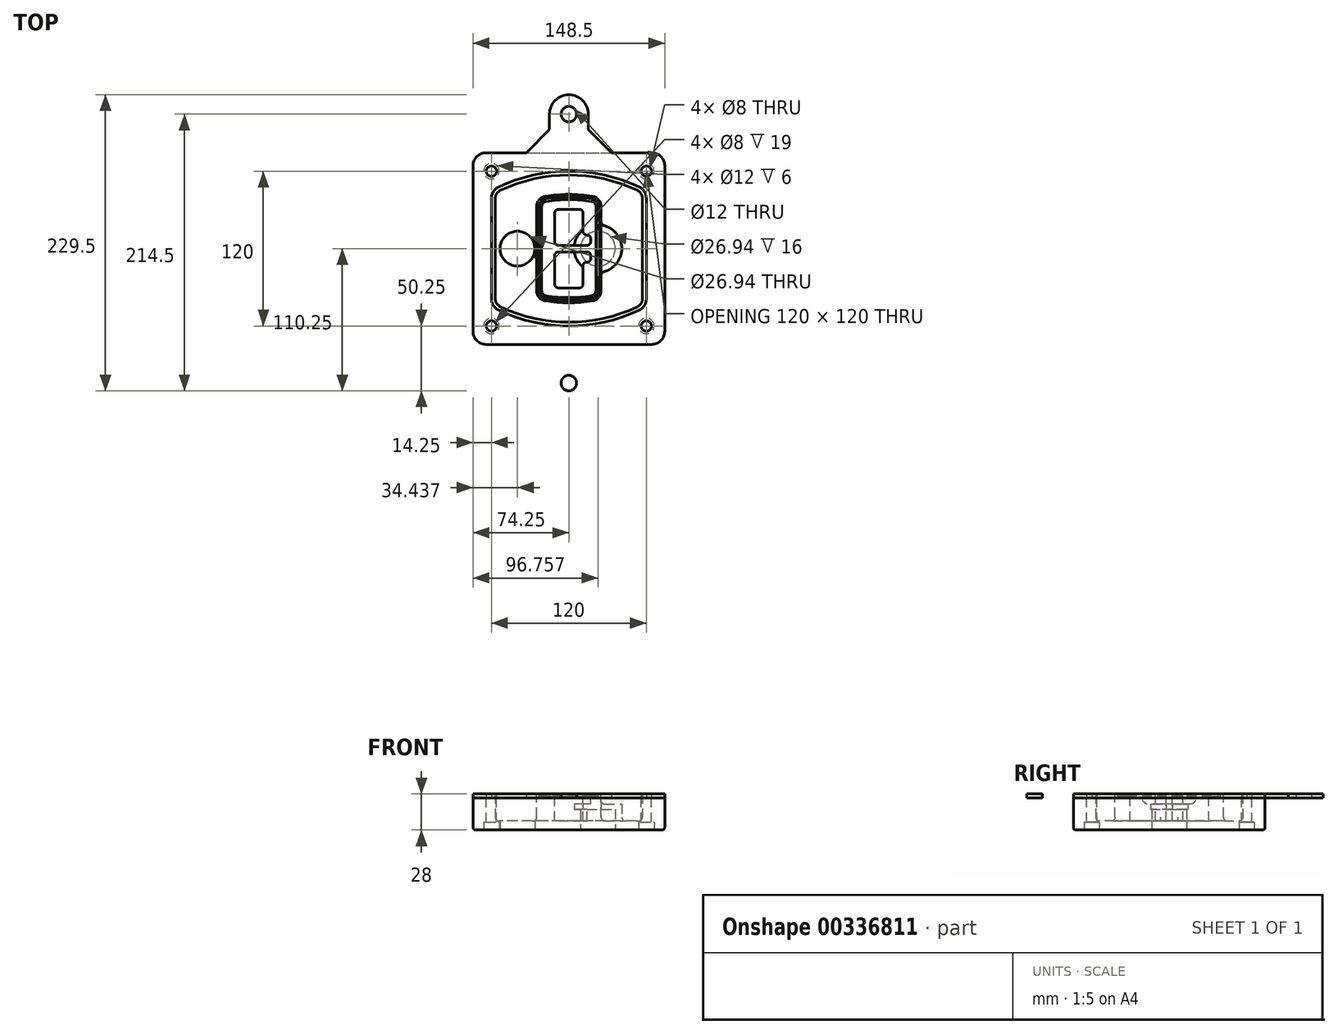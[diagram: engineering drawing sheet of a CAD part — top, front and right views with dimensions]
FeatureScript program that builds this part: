
annotation { "Feature Type Name" : "Feature", "Feature Type Description" : "" }
export const myFeature = defineFeature(function(context is Context, id is Id, definition is map)
    precondition{}
    {
        {
            var Q0;
            Q0=qCreatedBy(makeId("Top.planeOp"),FACE);
            var sketch = newSketch(context, id + "F0", { "sketchPlane" : qUnion([Q0])});
            skPoint(sketch, "E0.rect.middle", {"position": v(0, 0) * mm});
            skLineSegment(sketch, "E1.bottom", {"start": v(-64.25, -74.25) * mm, "end": v(64.25, -74.25) * mm});
            skLineSegment(sketch, "E1.top", {"start": v(-64.25, 74.25) * mm, "end": v(64.25, 74.25) * mm});
            skLineSegment(sketch, "E1.left", {"start": v(-74.25, -64.25) * mm, "end": v(-74.25, 64.25) * mm});
            skLineSegment(sketch, "E1.right", {"start": v(74.25, -64.25) * mm, "end": v(74.25, 64.25) * mm});
            skLineSegment(sketch, "E2", {"start": v(-74.25, 74.25) * mm, "end": v(74.25, -74.25) * mm, "construction": true});
            skLineSegment(sketch, "E3", {"start": v(74.25, 74.25) * mm, "end": v(-74.25, -74.25) * mm, "construction": true});
            skCircle(sketch, "E4", {"center": v(-60, 60) * mm, "radius": 4 * mm});
            skCircle(sketch, "E5", {"center": v(60, 60) * mm, "radius": 4 * mm});
            skCircle(sketch, "E6", {"center": v(60, -60) * mm, "radius": 4 * mm});
            skCircle(sketch, "E7", {"center": v(-60, -60) * mm, "radius": 4 * mm});
            skLineSegment(sketch, "E8", {"start": v(-60, 60) * mm, "end": v(60, 60) * mm, "construction": true});
            skLineSegment(sketch, "E9", {"start": v(60, 60) * mm, "end": v(60, -60) * mm, "construction": true});
            skLineSegment(sketch, "E10", {"start": v(60, -60) * mm, "end": v(-60, -60) * mm, "construction": true});
            skLineSegment(sketch, "E11", {"start": v(-60, -60) * mm, "end": v(-60, 60) * mm, "construction": true});
            skLineSegment(sketch, "E12", {"start": v(-60, 38.83) * mm, "end": v(-60, -38.83) * mm});
            skLineSegment(sketch, "E13", {"start": v(60, 38.83) * mm, "end": v(60, -38.83) * mm});
            skArc(sketch, "E14", {"start": v(54.26, 47.88) * mm, "mid": v(0, 60) * mm, "end": v(-54.26, 47.88) * mm});
            skArc(sketch, "E15", {"start": v(-54.26, -47.88) * mm, "mid": v(0, -60) * mm, "end": v(54.26, -47.88) * mm});
            skLineSegment(sketch, "E16", {"start": v(-60, 0) * mm, "end": v(60, 0) * mm, "construction": true});
            skPoint(sketch, "E17.visualSharp", {"position": v(-60, -45) * mm});
            skArc(sketch, "E17.filletArc", {"start": v(-60, -38.83) * mm, "mid": v(-58.44, -44.2) * mm, "end": v(-54.26, -47.88) * mm});
            skPoint(sketch, "E18.visualSharp", {"position": v(-60, 45) * mm});
            skArc(sketch, "E18.filletArc", {"start": v(-54.26, 47.88) * mm, "mid": v(-58.44, 44.2) * mm, "end": v(-60, 38.83) * mm});
            skPoint(sketch, "E19.visualSharp", {"position": v(60, 45) * mm});
            skArc(sketch, "E19.filletArc", {"start": v(60, 38.83) * mm, "mid": v(58.44, 44.2) * mm, "end": v(54.26, 47.88) * mm});
            skPoint(sketch, "E20.visualSharp", {"position": v(60, -45) * mm});
            skArc(sketch, "E20.filletArc", {"start": v(54.26, -47.88) * mm, "mid": v(58.44, -44.2) * mm, "end": v(60, -38.83) * mm});
            skPoint(sketch, "E21.visualSharp", {"position": v(-74.25, 74.25) * mm});
            skArc(sketch, "E21.filletArc", {"start": v(-64.25, 74.25) * mm, "mid": v(-71.32, 71.32) * mm, "end": v(-74.25, 64.25) * mm});
            skPoint(sketch, "E22.visualSharp", {"position": v(74.25, 74.25) * mm});
            skArc(sketch, "E22.filletArc", {"start": v(74.25, 64.25) * mm, "mid": v(71.32, 71.32) * mm, "end": v(64.25, 74.25) * mm});
            skPoint(sketch, "E23.visualSharp", {"position": v(74.25, -74.25) * mm});
            skArc(sketch, "E23.filletArc", {"start": v(64.25, -74.25) * mm, "mid": v(71.32, -71.32) * mm, "end": v(74.25, -64.25) * mm});
            skPoint(sketch, "E24.visualSharp", {"position": v(-74.25, -74.25) * mm});
            skArc(sketch, "E24.filletArc", {"start": v(-74.25, -64.25) * mm, "mid": v(-71.32, -71.32) * mm, "end": v(-64.25, -74.25) * mm});
            skArc(sketch, "E25.0", {"start": v(57, 38.83) * mm, "mid": v(55.9, 42.58) * mm, "end": v(52.98, 45.17) * mm});
            skLineSegment(sketch, "E25.1", {"start": v(57, 38.83) * mm, "end": v(57, -38.83) * mm});
            skArc(sketch, "E25.2", {"start": v(52.98, -45.17) * mm, "mid": v(55.9, -42.58) * mm, "end": v(57, -38.83) * mm});
            skArc(sketch, "E25.3", {"start": v(-52.98, -45.17) * mm, "mid": v(0, -57) * mm, "end": v(52.98, -45.17) * mm});
            skArc(sketch, "E25.4", {"start": v(-57, -38.83) * mm, "mid": v(-55.9, -42.58) * mm, "end": v(-52.98, -45.17) * mm});
            skArc(sketch, "E25.5", {"start": v(52.98, 45.17) * mm, "mid": v(0, 57) * mm, "end": v(-52.98, 45.17) * mm});
            skLineSegment(sketch, "E25.6", {"start": v(-57, 38.83) * mm, "end": v(-57, -38.83) * mm});
            skArc(sketch, "E25.7", {"start": v(-52.98, 45.17) * mm, "mid": v(-55.9, 42.58) * mm, "end": v(-57, 38.83) * mm});
            skArc(sketch, "E26.0", {"start": v(-55.96, 51.5) * mm, "mid": v(-61.82, 46.33) * mm, "end": v(-64, 38.83) * mm});
            skArc(sketch, "E26.1", {"start": v(55.96, 51.5) * mm, "mid": v(0, 64) * mm, "end": v(-55.96, 51.5) * mm});
            skArc(sketch, "E26.2", {"start": v(64, 38.83) * mm, "mid": v(61.82, 46.33) * mm, "end": v(55.96, 51.5) * mm});
            skLineSegment(sketch, "E26.3", {"start": v(64, 38.83) * mm, "end": v(64, -38.83) * mm});
            skArc(sketch, "E26.4", {"start": v(55.96, -51.5) * mm, "mid": v(61.82, -46.33) * mm, "end": v(64, -38.83) * mm});
            skLineSegment(sketch, "E26.5", {"start": v(-64, 38.83) * mm, "end": v(-64, -38.83) * mm});
            skArc(sketch, "E26.6", {"start": v(-55.96, -51.5) * mm, "mid": v(0, -64) * mm, "end": v(55.96, -51.5) * mm});
            skArc(sketch, "E26.7", {"start": v(-64, -38.83) * mm, "mid": v(-61.82, -46.33) * mm, "end": v(-55.96, -51.5) * mm});
            skSolve(sketch);
        }
        {
            var Q0;
            Q0=makeQuery(id+"F0.imprint","IMPRINT",FACE,{"disambiguationData":[TD([[makeQuery(id+"F0.imprint","IMPRINT",EDGE,{"derivedFrom":sQuery(id+"F0.wireOp",EDGE,"E1.bottom")}),1.0]])]});
            var Q1;
            Q1=makeQuery(id+"F0.imprint","IMPRINT",FACE,{"disambiguationData":[TD([[makeQuery(id+"F0.imprint","IMPRINT",EDGE,{"derivedFrom":sQuery(id+"F0.wireOp",EDGE,"E12")}),1.0]])]});
            var Q2;
            Q2=makeQuery(id+"F0.imprint","IMPRINT",FACE,{"disambiguationData":[TD([[makeQuery(id+"F0.imprint","IMPRINT",EDGE,{"derivedFrom":sQuery(id+"F0.wireOp",EDGE,"E25.0")}),1.0]])]});
            var Q3;
            Q3=makeQuery(id+"F0.imprint","IMPRINT",FACE,{"disambiguationData":[TD([[makeQuery(id+"F0.imprint","IMPRINT",EDGE,{"derivedFrom":sQuery(id+"F0.wireOp",EDGE,"E12")}),-1.0]])]});
            extrude(context, id + "F1", {"entities" : qUnion([Q0, Q1, Q2, Q3]), "oppositeDirection" : true, "depth" : 25 * mm});
        }
        {
            var Q0;
            Q0=makeQuery(id+"F0.imprint","IMPRINT",FACE,{"disambiguationData":[TD([[makeQuery(id+"F0.imprint","IMPRINT",EDGE,{"derivedFrom":sQuery(id+"F0.wireOp",EDGE,"E12")}),1.0]])]});
            extrude(context, id + "F2", {"entities" : qUnion([Q0]), "operationType" : NewBodyOperationType.ADD, "depth" : 3 * mm});
        }
        {
            var Q0;
            Q0=makeQuery(id+"F0.imprint","IMPRINT",FACE,{"disambiguationData":[TD([[makeQuery(id+"F0.imprint","IMPRINT",EDGE,{"derivedFrom":sQuery(id+"F0.wireOp",EDGE,"E25.0")}),1.0]])]});
            extrude(context, id + "F3", {"entities" : qUnion([Q0]), "operationType" : NewBodyOperationType.REMOVE, "oppositeDirection" : true, "depth" : 18 * mm});
        }
        {
            var Q0;
            Q0=makeQuery(id+"F2.opExtrude","CAP_FACE",FACE,{"disambiguationData":[OSD([sQuery(id+"F0.wireOp",EDGE,"E12"),sQuery(id+"F0.wireOp",EDGE,"E13"),sQuery(id+"F0.wireOp",EDGE,"E14"),sQuery(id+"F0.wireOp",EDGE,"E15"),sQuery(id+"F0.wireOp",EDGE,"E17.filletArc"),sQuery(id+"F0.wireOp",EDGE,"E18.filletArc"),sQuery(id+"F0.wireOp",EDGE,"E19.filletArc"),sQuery(id+"F0.wireOp",EDGE,"E20.filletArc"),sQuery(id+"F0.wireOp",EDGE,"E25.0"),sQuery(id+"F0.wireOp",EDGE,"E25.1"),sQuery(id+"F0.wireOp",EDGE,"E25.2"),sQuery(id+"F0.wireOp",EDGE,"E25.3"),sQuery(id+"F0.wireOp",EDGE,"E25.4"),sQuery(id+"F0.wireOp",EDGE,"E25.5"),sQuery(id+"F0.wireOp",EDGE,"E25.6"),sQuery(id+"F0.wireOp",EDGE,"E25.7")])],"isStart":false});
            var sketch = newSketch(context, id + "F4", { "sketchPlane" : qUnion([Q0])});
            skArc(sketch, "E27.0", {"start": v(-18.34, -40.45) * mm, "mid": v(0, -42) * mm, "end": v(18.34, -40.45) * mm});
            skArc(sketch, "E28.0", {"start": v(18.34, 40.45) * mm, "mid": v(0, 42) * mm, "end": v(-18.34, 40.45) * mm});
            skLineSegment(sketch, "E29", {"start": v(-25, 32.57) * mm, "end": v(-25, -32.57) * mm});
            skLineSegment(sketch, "E30", {"start": v(25, 32.57) * mm, "end": v(25, -32.57) * mm});
            skLineSegment(sketch, "E31", {"start": v(-25, 39.1) * mm, "end": v(25, 39.1) * mm, "construction": true});
            skLineSegment(sketch, "E32", {"start": v(-25, -39.1) * mm, "end": v(25, -39.1) * mm, "construction": true});
            skPoint(sketch, "E33.visualSharp", {"position": v(-25, 39.1) * mm});
            skArc(sketch, "E33.filletArc", {"start": v(-18.34, 40.45) * mm, "mid": v(-23.11, 37.73) * mm, "end": v(-25, 32.57) * mm});
            skPoint(sketch, "E34.visualSharp", {"position": v(25, 39.1) * mm});
            skArc(sketch, "E34.filletArc", {"start": v(25, 32.57) * mm, "mid": v(23.11, 37.73) * mm, "end": v(18.34, 40.45) * mm});
            skPoint(sketch, "E35.visualSharp", {"position": v(25, -39.1) * mm});
            skArc(sketch, "E35.filletArc", {"start": v(18.34, -40.45) * mm, "mid": v(23.11, -37.73) * mm, "end": v(25, -32.57) * mm});
            skPoint(sketch, "E36.visualSharp", {"position": v(-25, -39.1) * mm});
            skArc(sketch, "E36.filletArc", {"start": v(-25, -32.57) * mm, "mid": v(-23.11, -37.73) * mm, "end": v(-18.34, -40.45) * mm});
            skArc(sketch, "E37.0", {"start": v(52.98, 45.17) * mm, "mid": v(0, 57) * mm, "end": v(-52.98, 45.17) * mm});
            skArc(sketch, "E37.1", {"start": v(-52.98, 45.17) * mm, "mid": v(-55.9, 42.58) * mm, "end": v(-57, 38.83) * mm});
            skLineSegment(sketch, "E37.2", {"start": v(-57, 38.83) * mm, "end": v(-57, -38.83) * mm});
            skArc(sketch, "E37.3", {"start": v(-57, -38.83) * mm, "mid": v(-55.9, -42.58) * mm, "end": v(-52.98, -45.17) * mm});
            skArc(sketch, "E37.4", {"start": v(-52.98, -45.17) * mm, "mid": v(0, -57) * mm, "end": v(52.98, -45.17) * mm});
            skArc(sketch, "E37.5", {"start": v(52.98, -45.17) * mm, "mid": v(55.9, -42.58) * mm, "end": v(57, -38.83) * mm});
            skLineSegment(sketch, "E37.6", {"start": v(57, 38.83) * mm, "end": v(57, -38.83) * mm});
            skArc(sketch, "E37.7", {"start": v(57, 38.83) * mm, "mid": v(55.9, 42.58) * mm, "end": v(52.98, 45.17) * mm});
            skLineSegment(sketch, "E38.0", {"start": v(23, 32.57) * mm, "end": v(23, -32.57) * mm});
            skArc(sketch, "E38.1", {"start": v(18, -38.48) * mm, "mid": v(21.58, -36.44) * mm, "end": v(23, -32.57) * mm});
            skArc(sketch, "E38.2", {"start": v(-18, -38.48) * mm, "mid": v(0, -40) * mm, "end": v(18, -38.48) * mm});
            skArc(sketch, "E38.3", {"start": v(-23, -32.57) * mm, "mid": v(-21.58, -36.44) * mm, "end": v(-18, -38.48) * mm});
            skLineSegment(sketch, "E38.4", {"start": v(-23, 32.57) * mm, "end": v(-23, -32.57) * mm});
            skArc(sketch, "E38.5", {"start": v(23, 32.57) * mm, "mid": v(21.58, 36.44) * mm, "end": v(18, 38.48) * mm});
            skArc(sketch, "E38.6", {"start": v(-18, 38.48) * mm, "mid": v(-21.58, 36.44) * mm, "end": v(-23, 32.57) * mm});
            skArc(sketch, "E38.7", {"start": v(18, 38.48) * mm, "mid": v(0, 40) * mm, "end": v(-18, 38.48) * mm});
            skArc(sketch, "E39.0", {"start": v(21, 32.57) * mm, "mid": v(20.06, 35.15) * mm, "end": v(17.67, 36.5) * mm});
            skLineSegment(sketch, "E39.1", {"start": v(21, 32.57) * mm, "end": v(21, -32.57) * mm});
            skArc(sketch, "E39.2", {"start": v(17.67, -36.5) * mm, "mid": v(20.06, -35.15) * mm, "end": v(21, -32.57) * mm});
            skArc(sketch, "E39.3", {"start": v(-17.67, -36.5) * mm, "mid": v(0, -38) * mm, "end": v(17.67, -36.5) * mm});
            skArc(sketch, "E39.4", {"start": v(-21, -32.57) * mm, "mid": v(-20.06, -35.15) * mm, "end": v(-17.67, -36.5) * mm});
            skArc(sketch, "E39.5", {"start": v(17.67, 36.5) * mm, "mid": v(0, 38) * mm, "end": v(-17.67, 36.5) * mm});
            skLineSegment(sketch, "E39.6", {"start": v(-21, 32.57) * mm, "end": v(-21, -32.57) * mm});
            skArc(sketch, "E39.7", {"start": v(-17.67, 36.5) * mm, "mid": v(-20.06, 35.15) * mm, "end": v(-21, 32.57) * mm});
            skLineSegment(sketch, "E40", {"start": v(-25, 0) * mm, "end": v(25, 0) * mm, "construction": true});
            skLineSegment(sketch, "E41", {"start": v(-11, 5.5) * mm, "end": v(-11, 27.5) * mm});
            skLineSegment(sketch, "E42", {"start": v(-8, 30.5) * mm, "end": v(8, 30.5) * mm});
            skLineSegment(sketch, "E43", {"start": v(11, 27.5) * mm, "end": v(11, 13.5) * mm});
            skLineSegment(sketch, "E44", {"start": v(14, 10.5) * mm, "end": v(14, 10.5) * mm});
            skLineSegment(sketch, "E45", {"start": v(17, 7.5) * mm, "end": v(17, 5.5) * mm});
            skLineSegment(sketch, "E46", {"start": v(14, 2.5) * mm, "end": v(-8, 2.5) * mm});
            skPoint(sketch, "E47.visualSharp", {"position": v(-11, 30.5) * mm});
            skArc(sketch, "E47.filletArc", {"start": v(-8, 30.5) * mm, "mid": v(-10.12, 29.62) * mm, "end": v(-11, 27.5) * mm});
            skPoint(sketch, "E48.visualSharp", {"position": v(11, 30.5) * mm});
            skArc(sketch, "E48.filletArc", {"start": v(11, 27.5) * mm, "mid": v(10.12, 29.62) * mm, "end": v(8, 30.5) * mm});
            skPoint(sketch, "E49.visualSharp", {"position": v(11, 10.5) * mm});
            skArc(sketch, "E49.filletArc", {"start": v(11, 13.5) * mm, "mid": v(11.88, 11.38) * mm, "end": v(14, 10.5) * mm});
            skPoint(sketch, "E50.visualSharp", {"position": v(17, 10.5) * mm});
            skArc(sketch, "E50.filletArc", {"start": v(17, 7.5) * mm, "mid": v(16.12, 9.62) * mm, "end": v(14, 10.5) * mm});
            skPoint(sketch, "E51.visualSharp", {"position": v(17, 2.5) * mm});
            skArc(sketch, "E51.filletArc", {"start": v(14, 2.5) * mm, "mid": v(16.12, 3.38) * mm, "end": v(17, 5.5) * mm});
            skPoint(sketch, "E52.visualSharp", {"position": v(-11, 2.5) * mm});
            skArc(sketch, "E52.filletArc", {"start": v(-11, 5.5) * mm, "mid": v(-10.12, 3.38) * mm, "end": v(-8, 2.5) * mm});
            skLineSegment(sketch, "E53.0.MirrorCS", {"start": v(14, -2.5) * mm, "end": v(-8, -2.5) * mm});
            skArc(sketch, "E54.0.MirrorCS", {"start": v(-11, -5.5) * mm, "mid": v(-10.12, -3.38) * mm, "end": v(-8, -2.5) * mm});
            skLineSegment(sketch, "E55.0.MirrorCS", {"start": v(-11, -5.5) * mm, "end": v(-11, -27.5) * mm});
            skArc(sketch, "E56.0.MirrorCS", {"start": v(-8, -30.5) * mm, "mid": v(-10.12, -29.62) * mm, "end": v(-11, -27.5) * mm});
            skLineSegment(sketch, "E57.0.MirrorCS", {"start": v(-8, -30.5) * mm, "end": v(8, -30.5) * mm});
            skArc(sketch, "E58.0.MirrorCS", {"start": v(11, -27.5) * mm, "mid": v(10.12, -29.62) * mm, "end": v(8, -30.5) * mm});
            skLineSegment(sketch, "E59.0.MirrorCS", {"start": v(11, -27.5) * mm, "end": v(11, -13.5) * mm});
            skArc(sketch, "E60.0.MirrorCS", {"start": v(11, -13.5) * mm, "mid": v(11.88, -11.38) * mm, "end": v(14, -10.5) * mm});
            skArc(sketch, "E61.0.MirrorCS", {"start": v(17, -7.5) * mm, "mid": v(16.12, -9.62) * mm, "end": v(14, -10.5) * mm});
            skLineSegment(sketch, "E62.0.MirrorCS", {"start": v(17, -7.5) * mm, "end": v(17, -5.5) * mm});
            skArc(sketch, "E63.0.MirrorCS", {"start": v(14, -2.5) * mm, "mid": v(16.12, -3.38) * mm, "end": v(17, -5.5) * mm});
            skSolve(sketch);
        }
        {
            var Q0;
            Q0=makeQuery(id+"F4.imprint","IMPRINT",FACE,{"disambiguationData":[TD([[makeQuery(id+"F4.imprint","IMPRINT",EDGE,{"derivedFrom":sQuery(id+"F4.wireOp",EDGE,"E27.0")}),1.0]])]});
            var Q1;
            Q1=makeQuery(id+"F4.imprint","IMPRINT",FACE,{"disambiguationData":[TD([[makeQuery(id+"F4.imprint","IMPRINT",EDGE,{"derivedFrom":sQuery(id+"F4.wireOp",EDGE,"E38.0")}),-1.0]])]});
            var Q2;
            Q2=makeQuery(id+"F4.imprint","IMPRINT",FACE,{"disambiguationData":[TD([[makeQuery(id+"F4.imprint","IMPRINT",EDGE,{"derivedFrom":sQuery(id+"F4.wireOp",EDGE,"E39.0")}),1.0]])]});
            extrude(context, id + "F5", {"entities" : qUnion([Q0, Q1, Q2]), "operationType" : NewBodyOperationType.ADD, "endBound" : BoundingType.UP_TO_NEXT, "oppositeDirection" : true, "depth" : 25 * mm});
        }
        {
            var Q0;
            Q0=makeQuery(id+"F4.imprint","IMPRINT",FACE,{"disambiguationData":[TD([[makeQuery(id+"F4.imprint","IMPRINT",EDGE,{"derivedFrom":sQuery(id+"F4.wireOp",EDGE,"E38.0")}),-1.0]])]});
            extrude(context, id + "F6", {"entities" : qUnion([Q0]), "operationType" : NewBodyOperationType.REMOVE, "oppositeDirection" : true, "depth" : 2 * mm});
        }
        {
            var Q0;
            Q0=makeQuery(id+"F1.opExtrude","CAP_FACE",FACE,{"disambiguationData":[OSD([sQuery(id+"F0.wireOp",EDGE,"E1.bottom"),sQuery(id+"F0.wireOp",EDGE,"E1.top"),sQuery(id+"F0.wireOp",EDGE,"E1.left"),sQuery(id+"F0.wireOp",EDGE,"E1.right"),sQuery(id+"F0.wireOp",EDGE,"E4"),sQuery(id+"F0.wireOp",EDGE,"E5"),sQuery(id+"F0.wireOp",EDGE,"E6"),sQuery(id+"F0.wireOp",EDGE,"E7"),sQuery(id+"F0.wireOp",EDGE,"E21.filletArc"),sQuery(id+"F0.wireOp",EDGE,"E22.filletArc"),sQuery(id+"F0.wireOp",EDGE,"E23.filletArc"),sQuery(id+"F0.wireOp",EDGE,"E24.filletArc")])],"isStart":false});
            var sketch = newSketch(context, id + "F7", { "sketchPlane" : qUnion([Q0])});
            skCircle(sketch, "E64", {"center": v(22.5, 0) * mm, "radius": 13.47 * mm});
            skCircle(sketch, "E65", {"center": v(-39.81, 0) * mm, "radius": 13.47 * mm});
            skLineSegment(sketch, "E66", {"start": v(74.25, 0) * mm, "end": v(-74.25, 0) * mm});
            skCircle(sketch, "E67", {"center": v(22.5, 0) * mm, "radius": 18.47 * mm});
            skCircle(sketch, "E68", {"center": v(60, -60) * mm, "radius": 6 * mm});
            skCircle(sketch, "E69", {"center": v(-60, -60) * mm, "radius": 6 * mm});
            skCircle(sketch, "E70", {"center": v(-60, 60) * mm, "radius": 6 * mm});
            skCircle(sketch, "E71", {"center": v(60, 60) * mm, "radius": 6 * mm});
            skSolve(sketch);
        }
        {
            var Q0;
            {var subQ1=sQuery(id+"F7.wireOp",EDGE,"E66");var subQ4=sQuery(id+"F7.wireOp",EDGE,"E64");var subQ6=makeQuery(id+"F7.imprint","INTERSECT",VERTEX,{"disambiguationData":[OD(0.0)],"derivedFrom":[subQ4,subQ1]});Q0=makeQuery(id+"F7.imprint","IMPRINT",FACE,{"disambiguationData":[TD([[makeQuery(id+"F7.imprint","IMPRINT",EDGE,{"disambiguationData":[TD([[subQ6,-1.0]])],"derivedFrom":subQ4}),-1.0]])]});}
            var Q1;
            {var subQ0=sQuery(id+"F7.wireOp",EDGE,"E66");var subQ1=sQuery(id+"F7.wireOp",EDGE,"E64");var subQ3=makeQuery(id+"F7.imprint","INTERSECT",VERTEX,{"disambiguationData":[OD(0.0)],"derivedFrom":[subQ1,subQ0]});Q1=makeQuery(id+"F7.imprint","IMPRINT",FACE,{"disambiguationData":[TD([[makeQuery(id+"F7.imprint","IMPRINT",EDGE,{"disambiguationData":[TD([[subQ3,-1.0]])],"derivedFrom":subQ1}),1.0]])]});}
            var Q2;
            {var subQ0=sQuery(id+"F7.wireOp",EDGE,"E66");var subQ1=sQuery(id+"F7.wireOp",EDGE,"E64");var subQ3=makeQuery(id+"F7.imprint","INTERSECT",VERTEX,{"disambiguationData":[OD(0.0)],"derivedFrom":[subQ1,subQ0]});Q2=makeQuery(id+"F7.imprint","IMPRINT",FACE,{"disambiguationData":[TD([[makeQuery(id+"F7.imprint","IMPRINT",EDGE,{"disambiguationData":[TD([[subQ3,1.0]])],"derivedFrom":subQ1}),1.0]])]});}
            var Q3;
            {var subQ1=sQuery(id+"F7.wireOp",EDGE,"E66");var subQ4=sQuery(id+"F7.wireOp",EDGE,"E64");var subQ6=makeQuery(id+"F7.imprint","INTERSECT",VERTEX,{"disambiguationData":[OD(0.0)],"derivedFrom":[subQ4,subQ1]});Q3=makeQuery(id+"F7.imprint","IMPRINT",FACE,{"disambiguationData":[TD([[makeQuery(id+"F7.imprint","IMPRINT",EDGE,{"disambiguationData":[TD([[subQ6,1.0]])],"derivedFrom":subQ4}),-1.0]])]});}
            extrude(context, id + "F8", {"entities" : qUnion([Q0, Q1, Q2, Q3]), "operationType" : NewBodyOperationType.ADD, "oppositeDirection" : true, "depth" : 20 * mm});
        }
        {
            var Q0;
            {var subQ0=sQuery(id+"F7.wireOp",EDGE,"E66");var subQ1=sQuery(id+"F7.wireOp",EDGE,"E64");var subQ3=makeQuery(id+"F7.imprint","INTERSECT",VERTEX,{"disambiguationData":[OD(0.0)],"derivedFrom":[subQ1,subQ0]});Q0=makeQuery(id+"F7.imprint","IMPRINT",FACE,{"disambiguationData":[TD([[makeQuery(id+"F7.imprint","IMPRINT",EDGE,{"disambiguationData":[TD([[subQ3,-1.0]])],"derivedFrom":subQ1}),1.0]])]});}
            var Q1;
            {var subQ0=sQuery(id+"F7.wireOp",EDGE,"E66");var subQ1=sQuery(id+"F7.wireOp",EDGE,"E64");var subQ3=makeQuery(id+"F7.imprint","INTERSECT",VERTEX,{"disambiguationData":[OD(0.0)],"derivedFrom":[subQ1,subQ0]});Q1=makeQuery(id+"F7.imprint","IMPRINT",FACE,{"disambiguationData":[TD([[makeQuery(id+"F7.imprint","IMPRINT",EDGE,{"disambiguationData":[TD([[subQ3,1.0]])],"derivedFrom":subQ1}),1.0]])]});}
            extrude(context, id + "F9", {"entities" : qUnion([Q0, Q1]), "operationType" : NewBodyOperationType.REMOVE, "oppositeDirection" : true, "depth" : 16 * mm});
        }
        {
            var Q0;
            {var subQ0=sQuery(id+"F7.wireOp",EDGE,"E66");var subQ1=sQuery(id+"F7.wireOp",EDGE,"E65");var subQ3=makeQuery(id+"F7.imprint","INTERSECT",VERTEX,{"disambiguationData":[OD(0.0)],"derivedFrom":[subQ1,subQ0]});Q0=makeQuery(id+"F7.imprint","IMPRINT",FACE,{"disambiguationData":[TD([[makeQuery(id+"F7.imprint","IMPRINT",EDGE,{"disambiguationData":[TD([[subQ3,-1.0]])],"derivedFrom":subQ1}),1.0]])]});}
            var Q1;
            {var subQ0=sQuery(id+"F7.wireOp",EDGE,"E66");var subQ1=sQuery(id+"F7.wireOp",EDGE,"E65");var subQ3=makeQuery(id+"F7.imprint","INTERSECT",VERTEX,{"disambiguationData":[OD(0.0)],"derivedFrom":[subQ1,subQ0]});Q1=makeQuery(id+"F7.imprint","IMPRINT",FACE,{"disambiguationData":[TD([[makeQuery(id+"F7.imprint","IMPRINT",EDGE,{"disambiguationData":[TD([[subQ3,1.0]])],"derivedFrom":subQ1}),1.0]])]});}
            extrude(context, id + "F10", {"entities" : qUnion([Q0, Q1]), "operationType" : NewBodyOperationType.REMOVE, "oppositeDirection" : true, "depth" : 25 * mm});
        }
        {
            var Q0;
            Q0=makeQuery(id+"F7.imprint","IMPRINT",FACE,{"disambiguationData":[TD([[makeQuery(id+"F7.imprint","IMPRINT",EDGE,{"derivedFrom":sQuery(id+"F7.wireOp",EDGE,"E68")}),1.0]])]});
            var Q1;
            Q1=makeQuery(id+"F7.imprint","IMPRINT",FACE,{"disambiguationData":[TD([[makeQuery(id+"F7.imprint","IMPRINT",EDGE,{"derivedFrom":makeQuery(id+"F1.opExtrude","CAP_EDGE",EDGE,{"disambiguationData":[OSD([sQuery(id+"F0.wireOp",EDGE,"E5")])],"isStart":false})}),-1.0]])]});
            var Q2;
            Q2=makeQuery(id+"F7.imprint","IMPRINT",FACE,{"disambiguationData":[TD([[makeQuery(id+"F7.imprint","IMPRINT",EDGE,{"derivedFrom":sQuery(id+"F7.wireOp",EDGE,"E69")}),1.0]])]});
            var Q3;
            Q3=makeQuery(id+"F7.imprint","IMPRINT",FACE,{"disambiguationData":[TD([[makeQuery(id+"F7.imprint","IMPRINT",EDGE,{"derivedFrom":makeQuery(id+"F1.opExtrude","CAP_EDGE",EDGE,{"disambiguationData":[OSD([sQuery(id+"F0.wireOp",EDGE,"E4")])],"isStart":false})}),-1.0]])]});
            var Q4;
            Q4=makeQuery(id+"F7.imprint","IMPRINT",FACE,{"disambiguationData":[TD([[makeQuery(id+"F7.imprint","IMPRINT",EDGE,{"derivedFrom":sQuery(id+"F7.wireOp",EDGE,"E70")}),1.0]])]});
            var Q5;
            Q5=makeQuery(id+"F7.imprint","IMPRINT",FACE,{"disambiguationData":[TD([[makeQuery(id+"F7.imprint","IMPRINT",EDGE,{"derivedFrom":makeQuery(id+"F1.opExtrude","CAP_EDGE",EDGE,{"disambiguationData":[OSD([sQuery(id+"F0.wireOp",EDGE,"E7")])],"isStart":false})}),-1.0]])]});
            var Q6;
            Q6=makeQuery(id+"F7.imprint","IMPRINT",FACE,{"disambiguationData":[TD([[makeQuery(id+"F7.imprint","IMPRINT",EDGE,{"derivedFrom":sQuery(id+"F7.wireOp",EDGE,"E71")}),1.0]])]});
            var Q7;
            Q7=makeQuery(id+"F7.imprint","IMPRINT",FACE,{"disambiguationData":[TD([[makeQuery(id+"F7.imprint","IMPRINT",EDGE,{"derivedFrom":makeQuery(id+"F1.opExtrude","CAP_EDGE",EDGE,{"disambiguationData":[OSD([sQuery(id+"F0.wireOp",EDGE,"E6")])],"isStart":false})}),-1.0]])]});
            extrude(context, id + "F11", {"entities" : qUnion([Q0, Q1, Q2, Q3, Q4, Q5, Q6, Q7]), "operationType" : NewBodyOperationType.REMOVE, "oppositeDirection" : true, "depth" : 6 * mm});
        }
        {
            var Q0;
            Q0=makeQuery(id+"F9.boolean.opBoolean","COPY",FACE,{"derivedFrom":makeQuery(id+"F9.opExtrude","CAP_FACE",FACE,{"disambiguationData":[OSD([sQuery(id+"F7.wireOp",EDGE,"E64")])],"isStart":false})});
            var sketch = newSketch(context, id + "F12", { "sketchPlane" : qUnion([Q0])});
            skArc(sketch, "E72.0", {"start": v(11, 14.45) * mm, "mid": v(6.45, 9.13) * mm, "end": v(4.2, 2.5) * mm});
            skArc(sketch, "E72.1", {"start": v(4.2, -2.5) * mm, "mid": v(6.45, -9.13) * mm, "end": v(11, -14.45) * mm});
            skLineSegment(sketch, "E73", {"start": v(4.2, -2.5) * mm, "end": v(14, -2.5) * mm});
            skLineSegment(sketch, "E74.0", {"start": v(14, 2.5) * mm, "end": v(4.2, 2.5) * mm});
            skArc(sketch, "E74.1", {"start": v(14, 2.5) * mm, "mid": v(16.12, 3.38) * mm, "end": v(17, 5.5) * mm});
            skLineSegment(sketch, "E74.2", {"start": v(17, 7.5) * mm, "end": v(17, 5.5) * mm});
            skArc(sketch, "E74.3", {"start": v(17, 7.5) * mm, "mid": v(16.12, 9.62) * mm, "end": v(14, 10.5) * mm});
            skArc(sketch, "E74.4", {"start": v(11, 13.5) * mm, "mid": v(11.88, 11.38) * mm, "end": v(14, 10.5) * mm});
            skLineSegment(sketch, "E74.5", {"start": v(11, 14.45) * mm, "end": v(11, 13.5) * mm});
            skLineSegment(sketch, "E74.7", {"start": v(14, -2.5) * mm, "end": v(4.2, -2.5) * mm});
            skArc(sketch, "E74.8", {"start": v(14, -2.5) * mm, "mid": v(16.12, -3.38) * mm, "end": v(17, -5.5) * mm});
            skLineSegment(sketch, "E74.9", {"start": v(17, -7.5) * mm, "end": v(17, -5.5) * mm});
            skArc(sketch, "E74.10", {"start": v(17, -7.5) * mm, "mid": v(16.12, -9.62) * mm, "end": v(14, -10.5) * mm});
            skArc(sketch, "E74.11", {"start": v(11, -13.5) * mm, "mid": v(11.88, -11.38) * mm, "end": v(14, -10.5) * mm});
            skLineSegment(sketch, "E74.12", {"start": v(11, -14.45) * mm, "end": v(11, -13.5) * mm});
            skPoint(sketch, "E75.orphan", {"position": v(11, -27.5) * mm});
            skPoint(sketch, "E76.orphan", {"position": v(-8, -2.5) * mm});
            skPoint(sketch, "E77.orphan", {"position": v(-8, 2.5) * mm});
            skPoint(sketch, "E78.orphan", {"position": v(11, 27.5) * mm});
            skSolve(sketch);
        }
        {
            var Q0;
            {var subQ7=sQuery(id+"F12.wireOp",EDGE,"E72.0");var subQ14=sQuery(id+"F12.wireOp",EDGE,"E72.1");var subQ16=sQuery(id+"F12.wireOp",EDGE,"E74.1");var subQ18=sQuery(id+"F12.wireOp",EDGE,"E74.8");Q0=qUnion([makeQuery(id+"F12.imprint","IMPRINT",FACE,{"disambiguationData":[TD([[makeQuery(id+"F12.imprint","IMPRINT",EDGE,{"derivedFrom":subQ7}),1.0]])]}),makeQuery(id+"F12.imprint","IMPRINT",FACE,{"disambiguationData":[TD([[makeQuery(id+"F12.imprint","IMPRINT",EDGE,{"derivedFrom":subQ14}),1.0]])]}),makeQuery(id+"F12.imprint","IMPRINT",FACE,{"disambiguationData":[TD([[makeQuery(id+"F12.imprint","IMPRINT",EDGE,{"derivedFrom":subQ16}),1.0]])]}),makeQuery(id+"F12.imprint","IMPRINT",FACE,{"disambiguationData":[TD([[makeQuery(id+"F12.imprint","IMPRINT",EDGE,{"derivedFrom":subQ18}),-1.0]])]})]);}
            var Q1;
            Q1=makeQuery(id+"F5.boolean.opBoolean","SPLIT",FACE,{"disambiguationData":[TD([makeQuery(id+"F5.opExtrude","SWEPT_FACE",FACE,{"disambiguationData":[OSD([sQuery(id+"F4.wireOp",EDGE,"E41")])]})])],"derivedFrom":makeQuery(id+"F3.boolean.opBoolean","COPY",FACE,{"derivedFrom":makeQuery(id+"F3.opExtrude","CAP_FACE",FACE,{"disambiguationData":[OSD([sQuery(id+"F0.wireOp",EDGE,"E25.0"),sQuery(id+"F0.wireOp",EDGE,"E25.1"),sQuery(id+"F0.wireOp",EDGE,"E25.2"),sQuery(id+"F0.wireOp",EDGE,"E25.3"),sQuery(id+"F0.wireOp",EDGE,"E25.4"),sQuery(id+"F0.wireOp",EDGE,"E25.5"),sQuery(id+"F0.wireOp",EDGE,"E25.6"),sQuery(id+"F0.wireOp",EDGE,"E25.7")])],"isStart":false})})});
            extrude(context, id + "F13", {"entities" : qUnion([Q0]), "operationType" : NewBodyOperationType.REMOVE, "endBound" : BoundingType.UP_TO_SURFACE, "endBoundEntityFace" : qUnion([Q1]), "depth" : 25 * mm});
        }
        {
            var Q0;
            Q0=makeQuery(id+"F3.boolean.opBoolean","COPY",EDGE,{"derivedFrom":makeQuery(id+"F3.opExtrude","CAP_EDGE",EDGE,{"disambiguationData":[OSD([sQuery(id+"F0.wireOp",EDGE,"E25.6")])],"isStart":false})});
            var Q1;
            Q1=makeQuery(id+"F8.boolean.opBoolean","INTERSECT",EDGE,{"derivedFrom":[makeQuery(id+"F5.opExtrude","SWEPT_FACE",FACE,{"disambiguationData":[OSD([sQuery(id+"F4.wireOp",EDGE,"E30")])]}),makeQuery(id+"F8.opExtrude","CAP_FACE",FACE,{"disambiguationData":[OSD([sQuery(id+"F7.wireOp",EDGE,"E67")])],"isStart":false})]});
            var Q2;
            Q2=makeQuery(id+"F8.boolean.opBoolean","INTERSECT",EDGE,{"disambiguationData":[OD(1.0)],"derivedFrom":[makeQuery(id+"F5.opExtrude","SWEPT_FACE",FACE,{"disambiguationData":[OSD([sQuery(id+"F4.wireOp",EDGE,"E30")])]}),makeQuery(id+"F8.opExtrude","SWEPT_FACE",FACE,{"disambiguationData":[OSD([sQuery(id+"F7.wireOp",EDGE,"E67")])]})]});
            var Q3;
            {var subQ0=sQuery(id+"F4.wireOp",EDGE,"E30");Q3=makeQuery(id+"F8.boolean.opBoolean","SPLIT",EDGE,{"disambiguationData":[TD([makeQuery(id+"F5.opExtrude","SWEPT_FACE",FACE,{"disambiguationData":[OSD([sQuery(id+"F4.wireOp",EDGE,"E35.filletArc")])]})])],"derivedFrom":makeQuery(id+"F5.opExtrude","CAP_EDGE",EDGE,{"disambiguationData":[OSD([subQ0])],"isStart":false})});}
            var Q4;
            {var subQ0=sQuery(id+"F0.wireOp",EDGE,"E25.7");var subQ1=sQuery(id+"F0.wireOp",EDGE,"E25.1");var subQ2=sQuery(id+"F0.wireOp",EDGE,"E25.6");var subQ3=sQuery(id+"F0.wireOp",EDGE,"E25.5");var subQ4=sQuery(id+"F0.wireOp",EDGE,"E25.4");var subQ5=sQuery(id+"F0.wireOp",EDGE,"E25.0");var subQ6=sQuery(id+"F0.wireOp",EDGE,"E25.2");var subQ7=sQuery(id+"F0.wireOp",EDGE,"E25.3");Q4=makeQuery(id+"F8.boolean.opBoolean","INTERSECT",EDGE,{"derivedFrom":[makeQuery(id+"F5.boolean.opBoolean","SPLIT",FACE,{"disambiguationData":[TD([makeQuery(id+"F2.opExtrude","SWEPT_FACE",FACE,{"disambiguationData":[OSD([subQ5])]})])],"derivedFrom":makeQuery(id+"F3.boolean.opBoolean","COPY",FACE,{"derivedFrom":makeQuery(id+"F3.opExtrude","CAP_FACE",FACE,{"disambiguationData":[OSD([subQ5,subQ1,subQ6,subQ7,subQ4,subQ3,subQ2,subQ0])],"isStart":false})})}),makeQuery(id+"F8.opExtrude","SWEPT_FACE",FACE,{"disambiguationData":[OSD([sQuery(id+"F7.wireOp",EDGE,"E67")])]})]});}
            var Q5;
            Q5=makeQuery(id+"F8.boolean.opBoolean","INTERSECT",EDGE,{"disambiguationData":[OD(0.0)],"derivedFrom":[makeQuery(id+"F5.opExtrude","SWEPT_FACE",FACE,{"disambiguationData":[OSD([sQuery(id+"F4.wireOp",EDGE,"E30")])]}),makeQuery(id+"F8.opExtrude","SWEPT_FACE",FACE,{"disambiguationData":[OSD([sQuery(id+"F7.wireOp",EDGE,"E67")])]})]});
            fillet(context, id + "F14", {"entities" : qUnion([Q0, Q1, Q2, Q3, Q4, Q5]), "radius" : 3 * mm, "tangentPropagation" : true, "allowEdgeOverflow" : false});
        }
        {
            var Q0;
            Q0=makeQuery(id+"F1.opExtrude","CAP_EDGE",EDGE,{"disambiguationData":[OSD([sQuery(id+"F0.wireOp",EDGE,"E1.bottom")])],"isStart":false});
            fillet(context, id + "F15", {"entities" : qUnion([Q0]), "radius" : 2 * mm, "tangentPropagation" : true, "allowEdgeOverflow" : false});
        }
        {
            var Q0;
            {var subQ0=sQuery(id+"F0.wireOp",EDGE,"E21.filletArc");var subQ1=sQuery(id+"F0.wireOp",EDGE,"E7");var subQ2=sQuery(id+"F0.wireOp",EDGE,"E6");var subQ3=sQuery(id+"F0.wireOp",EDGE,"E5");var subQ4=sQuery(id+"F0.wireOp",EDGE,"E4");var subQ5=sQuery(id+"F0.wireOp",EDGE,"E22.filletArc");var subQ6=sQuery(id+"F0.wireOp",EDGE,"E1.bottom");var subQ7=sQuery(id+"F0.wireOp",EDGE,"E1.right");var subQ8=sQuery(id+"F0.wireOp",EDGE,"E1.top");var subQ9=sQuery(id+"F0.wireOp",EDGE,"E1.left");var subQ10=sQuery(id+"F0.wireOp",EDGE,"E23.filletArc");var subQ11=sQuery(id+"F0.wireOp",EDGE,"E24.filletArc");Q0=makeQuery(id+"F2.boolean.opBoolean","SPLIT",FACE,{"disambiguationData":[TD([makeQuery(id+"F1.opExtrude","SWEPT_FACE",FACE,{"disambiguationData":[OSD([subQ6])]})])],"derivedFrom":makeQuery(id+"F1.opExtrude","CAP_FACE",FACE,{"disambiguationData":[OSD([subQ6,subQ8,subQ9,subQ7,subQ4,subQ3,subQ2,subQ1,subQ0,subQ5,subQ10,subQ11])],"isStart":true})});}
            var sketch = newSketch(context, id + "F16", { "sketchPlane" : qUnion([Q0])});
            skLineSegment(sketch, "E79", {"start": v(0, 74.25) * mm, "end": v(0, 104.25) * mm, "construction": true});
            skLineSegment(sketch, "E80", {"start": v(-33, 74.25) * mm, "end": v(-15, 92.25) * mm});
            skLineSegment(sketch, "E81", {"start": v(-15, 92.25) * mm, "end": v(-15, 104.25) * mm});
            skLineSegment(sketch, "E82", {"start": v(33, 74.25) * mm, "end": v(15, 92.25) * mm});
            skLineSegment(sketch, "E83", {"start": v(15, 92.25) * mm, "end": v(15, 104.25) * mm});
            skArc(sketch, "E84", {"start": v(15, 104.25) * mm, "mid": v(0, 119.25) * mm, "end": v(-15, 104.25) * mm});
            skCircle(sketch, "E85", {"center": v(0, 104.25) * mm, "radius": 6 * mm});
            skLineSegment(sketch, "E86", {"start": v(0, 104.25) * mm, "end": v(-15, 104.25) * mm, "construction": true});
            skLineSegment(sketch, "E87", {"start": v(-74.25, 0) * mm, "end": v(74.25, 0) * mm, "construction": true});
            skLineSegment(sketch, "E88.MirrorCS", {"start": v(-33, -74.25) * mm, "end": v(-15, -92.25) * mm});
            skArc(sketch, "E89.MirrorCS", {"start": v(15, -104.25) * mm, "mid": v(0, -119.25) * mm, "end": v(-15, -104.25) * mm});
            skCircle(sketch, "E90.MirrorC", {"center": v(0, -104.25) * mm, "radius": 6 * mm});
            skLineSegment(sketch, "E91.MirrorCS", {"start": v(0, -104.25) * mm, "end": v(-15, -104.25) * mm, "construction": true});
            skLineSegment(sketch, "E92.MirrorCS", {"start": v(0, -74.25) * mm, "end": v(0, -104.25) * mm, "construction": true});
            skLineSegment(sketch, "E93.MirrorCS", {"start": v(-15, -92.25) * mm, "end": v(-15, -104.25) * mm});
            skLineSegment(sketch, "E94.MirrorCS", {"start": v(33, -74.25) * mm, "end": v(15, -92.25) * mm});
            skLineSegment(sketch, "E95.MirrorCS", {"start": v(15, -92.25) * mm, "end": v(15, -104.25) * mm});
            skSolve(sketch);
        }
        {
            var Q0;
            {var subQ1=sQuery(id+"F16.wireOp",EDGE,"E80");Q0=makeQuery(id+"F16.imprint","IMPRINT",FACE,{"disambiguationData":[TD([[makeQuery(id+"F16.imprint","IMPRINT",EDGE,{"derivedFrom":subQ1}),-1.0]])]});}
            var Q1;
            Q1=makeQuery(id+"F16.imprint","IMPRINT",FACE,{"disambiguationData":[TD([[makeQuery(id+"F16.imprint","IMPRINT",EDGE,{"derivedFrom":makeQuery(id+"F1.opExtrude","CAP_EDGE",EDGE,{"disambiguationData":[OSD([sQuery(id+"F0.wireOp",EDGE,"E1.left")])],"isStart":true})}),-1.0]])]});
            var Q2;
            Q2=makeQuery(id+"F16.imprint","IMPRINT",FACE,{"disambiguationData":[TD([[makeQuery(id+"F16.imprint","IMPRINT",EDGE,{"derivedFrom":sQuery(id+"F16.wireOp",EDGE,"E90.MirrorC")}),1.0]])]});
            var Q3;
            {var subQ0=sQuery(id+"F4.wireOp",EDGE,"E36.filletArc");var subQ1=sQuery(id+"F4.wireOp",EDGE,"E35.filletArc");var subQ2=sQuery(id+"F4.wireOp",EDGE,"E34.filletArc");var subQ3=sQuery(id+"F4.wireOp",EDGE,"E33.filletArc");var subQ4=sQuery(id+"F4.wireOp",EDGE,"E27.0");var subQ5=sQuery(id+"F4.wireOp",EDGE,"E30");var subQ6=sQuery(id+"F4.wireOp",EDGE,"E28.0");var subQ7=sQuery(id+"F4.wireOp",EDGE,"E29");Q3=makeQuery(id+"F6.boolean.opBoolean","SPLIT",FACE,{"disambiguationData":[TD([makeQuery(id+"F5.opExtrude","SWEPT_FACE",FACE,{"disambiguationData":[OSD([subQ4])]})])],"derivedFrom":makeQuery(id+"F5.opExtrude","CAP_FACE",FACE,{"disambiguationData":[OSD([subQ4,subQ6,subQ7,subQ5,subQ3,subQ2,subQ1,subQ0,sQuery(id+"F4.wireOp",EDGE,"E41"),sQuery(id+"F4.wireOp",EDGE,"E42"),sQuery(id+"F4.wireOp",EDGE,"E43"),sQuery(id+"F4.wireOp",EDGE,"E45"),sQuery(id+"F4.wireOp",EDGE,"E46"),sQuery(id+"F4.wireOp",EDGE,"E47.filletArc"),sQuery(id+"F4.wireOp",EDGE,"E48.filletArc"),sQuery(id+"F4.wireOp",EDGE,"E49.filletArc"),sQuery(id+"F4.wireOp",EDGE,"E50.filletArc"),sQuery(id+"F4.wireOp",EDGE,"E51.filletArc"),sQuery(id+"F4.wireOp",EDGE,"E52.filletArc"),sQuery(id+"F4.wireOp",EDGE,"E53.0.MirrorCS"),sQuery(id+"F4.wireOp",EDGE,"E54.0.MirrorCS"),sQuery(id+"F4.wireOp",EDGE,"E55.0.MirrorCS"),sQuery(id+"F4.wireOp",EDGE,"E56.0.MirrorCS"),sQuery(id+"F4.wireOp",EDGE,"E57.0.MirrorCS"),sQuery(id+"F4.wireOp",EDGE,"E58.0.MirrorCS"),sQuery(id+"F4.wireOp",EDGE,"E59.0.MirrorCS"),sQuery(id+"F4.wireOp",EDGE,"E60.0.MirrorCS"),sQuery(id+"F4.wireOp",EDGE,"E61.0.MirrorCS"),sQuery(id+"F4.wireOp",EDGE,"E62.0.MirrorCS"),sQuery(id+"F4.wireOp",EDGE,"E63.0.MirrorCS")])],"isStart":true})});}
            extrude(context, id + "F17", {"entities" : qUnion([Q0, Q1, Q2]), "endBound" : BoundingType.UP_TO_SURFACE, "endBoundEntityFace" : qUnion([Q3]), "depth" : 25 * mm});
        }
    });
